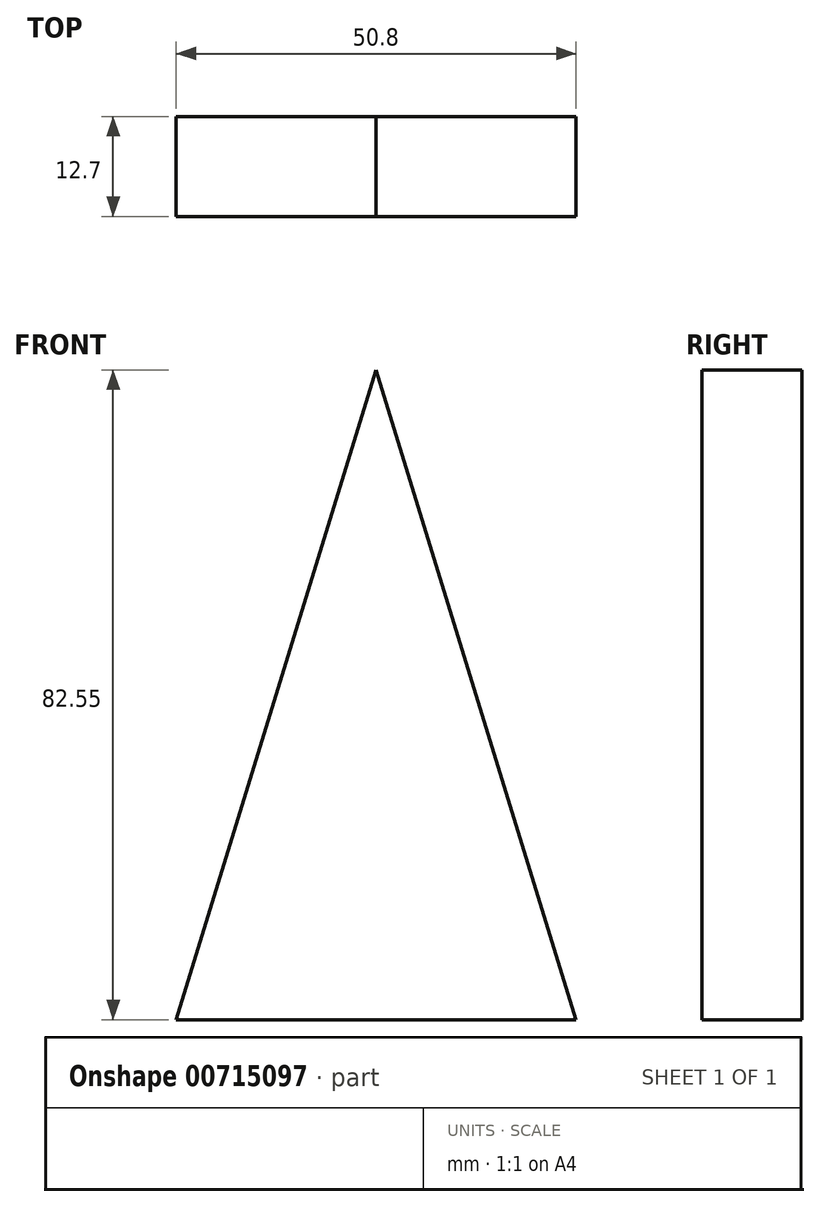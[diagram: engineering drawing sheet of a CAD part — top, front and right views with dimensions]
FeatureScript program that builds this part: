
annotation { "Feature Type Name" : "Feature", "Feature Type Description" : "" }
export const myFeature = defineFeature(function(context is Context, id is Id, definition is map)
    precondition{}
    {
        {
            var Q0;
            Q0=qCreatedBy(makeId("Front.planeOp"),FACE);
            var sketch = newSketch(context, id + "F0", { "sketchPlane" : qUnion([Q0])});
            skLineSegment(sketch, "E0.bottom", {"start": v(0, 0) * mm, "end": v(50.8, 0) * mm});
            skLineSegment(sketch, "E0.top", {"start": v(0, 82.55) * mm, "end": v(50.8, 82.55) * mm});
            skLineSegment(sketch, "E0.left", {"start": v(0, 0) * mm, "end": v(0, 82.55) * mm});
            skLineSegment(sketch, "E0.right", {"start": v(50.8, 0) * mm, "end": v(50.8, 82.55) * mm});
            skLineSegment(sketch, "E1", {"start": v(0, 0) * mm, "end": v(25.4, 82.55) * mm});
            skLineSegment(sketch, "E2", {"start": v(50.8, 0) * mm, "end": v(25.4, 82.55) * mm});
            skSolve(sketch);
        }
        {
            var Q0;
            Q0=makeQuery(id+"F0.imprint","IMPRINT",FACE,{"disambiguationData":[TD([[makeQuery(id+"F0.imprint","IMPRINT",EDGE,{"derivedFrom":sQuery(id+"F0.wireOp",EDGE,"E0.bottom")}),1.0]])]});
            extrude(context, id + "F1", {"entities" : qUnion([Q0]), "depth" : 12.7 * mm, "offsetDistance" : 25.4 * mm});
        }
    });
